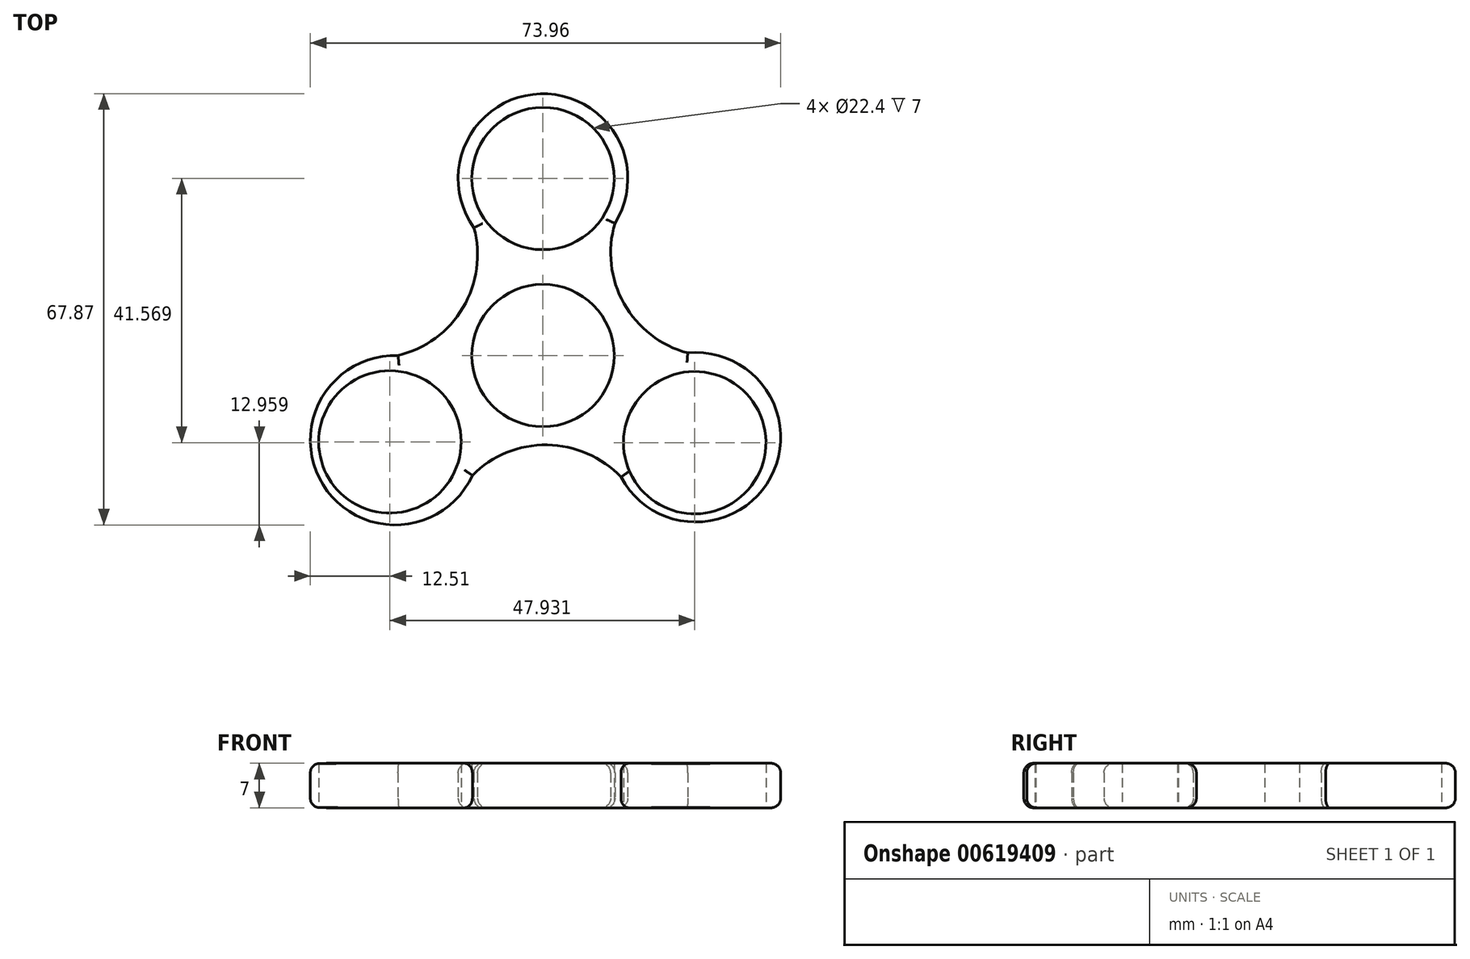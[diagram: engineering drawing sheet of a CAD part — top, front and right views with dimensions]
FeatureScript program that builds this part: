
annotation { "Feature Type Name" : "Feature", "Feature Type Description" : "" }
export const myFeature = defineFeature(function(context is Context, id is Id, definition is map)
    precondition{}
    {
        {
            var Q0;
            Q0=qCreatedBy(makeId("Top.planeOp"),FACE);
            var sketch = newSketch(context, id + "F0", { "sketchPlane" : qUnion([Q0])});
            skCircle(sketch, "E0", {"center": v(0, 0) * mm, "radius": 11.2 * mm});
            skCircle(sketch, "E1", {"center": v(0, 27.86) * mm, "radius": 11.2 * mm});
            skArc(sketch, "E2", {"start": v(11.32, 20.8) * mm, "mid": v(-0.41, 41.19) * mm, "end": v(-10.86, 20.11) * mm});
            skCircle(sketch, "E3.1.1", {"center": v(-24.07, -13.6) * mm, "radius": 11.2 * mm});
            skCircle(sketch, "E3.2.1", {"center": v(23.86, -13.71) * mm, "radius": 11.2 * mm});
            skPoint(sketch, "E3.center", {"position": v(-0.07, 0.19) * mm});
            skArc(sketch, "E4", {"start": v(11.32, 20.8) * mm, "mid": v(12.74, 8.19) * mm, "end": v(22.77, 0.41) * mm});
            skArc(sketch, "E5.1.0", {"start": v(-22.79, 0) * mm, "mid": v(-12.58, 7.54) * mm, "end": v(-10.86, 20.11) * mm});
            skArc(sketch, "E5.2.0", {"start": v(12.28, -19.14) * mm, "mid": v(0.64, -14.06) * mm, "end": v(-11.1, -18.86) * mm});
            skPoint(sketch, "E5.center", {"position": v(0.27, 0.55) * mm});
            skArc(sketch, "E6.1.0", {"start": v(-22.79, 0) * mm, "mid": v(-34.58, -20.35) * mm, "end": v(-11.1, -18.86) * mm});
            skArc(sketch, "E6.2.0", {"start": v(12.28, -19.14) * mm, "mid": v(35.8, -19.17) * mm, "end": v(22.77, 0.41) * mm});
            skSolve(sketch);
        }
        {
            var Q0;
            Q0 = qSketchRegion(id + "F0", true);
            extrude(context, id + "F1", {"entities" : qUnion([Q0]), "depth" : 7 * mm, "offsetDistance" : 25 * mm});
        }
        {
            var Q0;
            Q0=makeQuery(id+"F1.opExtrude","CAP_EDGE",EDGE,{"disambiguationData":[OSD([sQuery(id+"F0.wireOp",EDGE,"E5.2.0")])],"isStart":false});
            var Q1;
            Q1=makeQuery(id+"F1.opExtrude","CAP_EDGE",EDGE,{"disambiguationData":[OSD([sQuery(id+"F0.wireOp",EDGE,"E6.1.0")])],"isStart":false});
            var Q2;
            Q2=makeQuery(id+"F1.opExtrude","CAP_EDGE",EDGE,{"disambiguationData":[OSD([sQuery(id+"F0.wireOp",EDGE,"E5.1.0")])],"isStart":false});
            var Q3;
            Q3=makeQuery(id+"F1.opExtrude","CAP_EDGE",EDGE,{"disambiguationData":[OSD([sQuery(id+"F0.wireOp",EDGE,"E2")])],"isStart":false});
            var Q4;
            Q4=makeQuery(id+"F1.opExtrude","CAP_EDGE",EDGE,{"disambiguationData":[OSD([sQuery(id+"F0.wireOp",EDGE,"E4")])],"isStart":false});
            var Q5;
            Q5=makeQuery(id+"F1.opExtrude","CAP_EDGE",EDGE,{"disambiguationData":[OSD([sQuery(id+"F0.wireOp",EDGE,"E6.2.0")])],"isStart":false});
            fillet(context, id + "F2", {"entities" : qUnion([Q0, Q1, Q2, Q3, Q4, Q5]), "radius" : 1.5 * mm, "tangentPropagation" : true, "allowEdgeOverflow" : false});
        }
        {
            var Q0;
            Q0=makeQuery(id+"F1.opExtrude","CAP_EDGE",EDGE,{"disambiguationData":[OSD([sQuery(id+"F0.wireOp",EDGE,"E6.2.0")])],"isStart":true});
            var Q1;
            Q1=makeQuery(id+"F1.opExtrude","CAP_EDGE",EDGE,{"disambiguationData":[OSD([sQuery(id+"F0.wireOp",EDGE,"E5.2.0")])],"isStart":true});
            var Q2;
            Q2=makeQuery(id+"F1.opExtrude","CAP_EDGE",EDGE,{"disambiguationData":[OSD([sQuery(id+"F0.wireOp",EDGE,"E6.1.0")])],"isStart":true});
            var Q3;
            Q3=makeQuery(id+"F1.opExtrude","CAP_EDGE",EDGE,{"disambiguationData":[OSD([sQuery(id+"F0.wireOp",EDGE,"E5.1.0")])],"isStart":true});
            var Q4;
            Q4=makeQuery(id+"F1.opExtrude","CAP_EDGE",EDGE,{"disambiguationData":[OSD([sQuery(id+"F0.wireOp",EDGE,"E4")])],"isStart":true});
            var Q5;
            Q5=makeQuery(id+"F1.opExtrude","CAP_EDGE",EDGE,{"disambiguationData":[OSD([sQuery(id+"F0.wireOp",EDGE,"E2")])],"isStart":true});
            fillet(context, id + "F3", {"entities" : qUnion([Q0, Q1, Q2, Q3, Q4, Q5]), "radius" : 1.5 * mm, "tangentPropagation" : true, "allowEdgeOverflow" : false});
        }
    });
